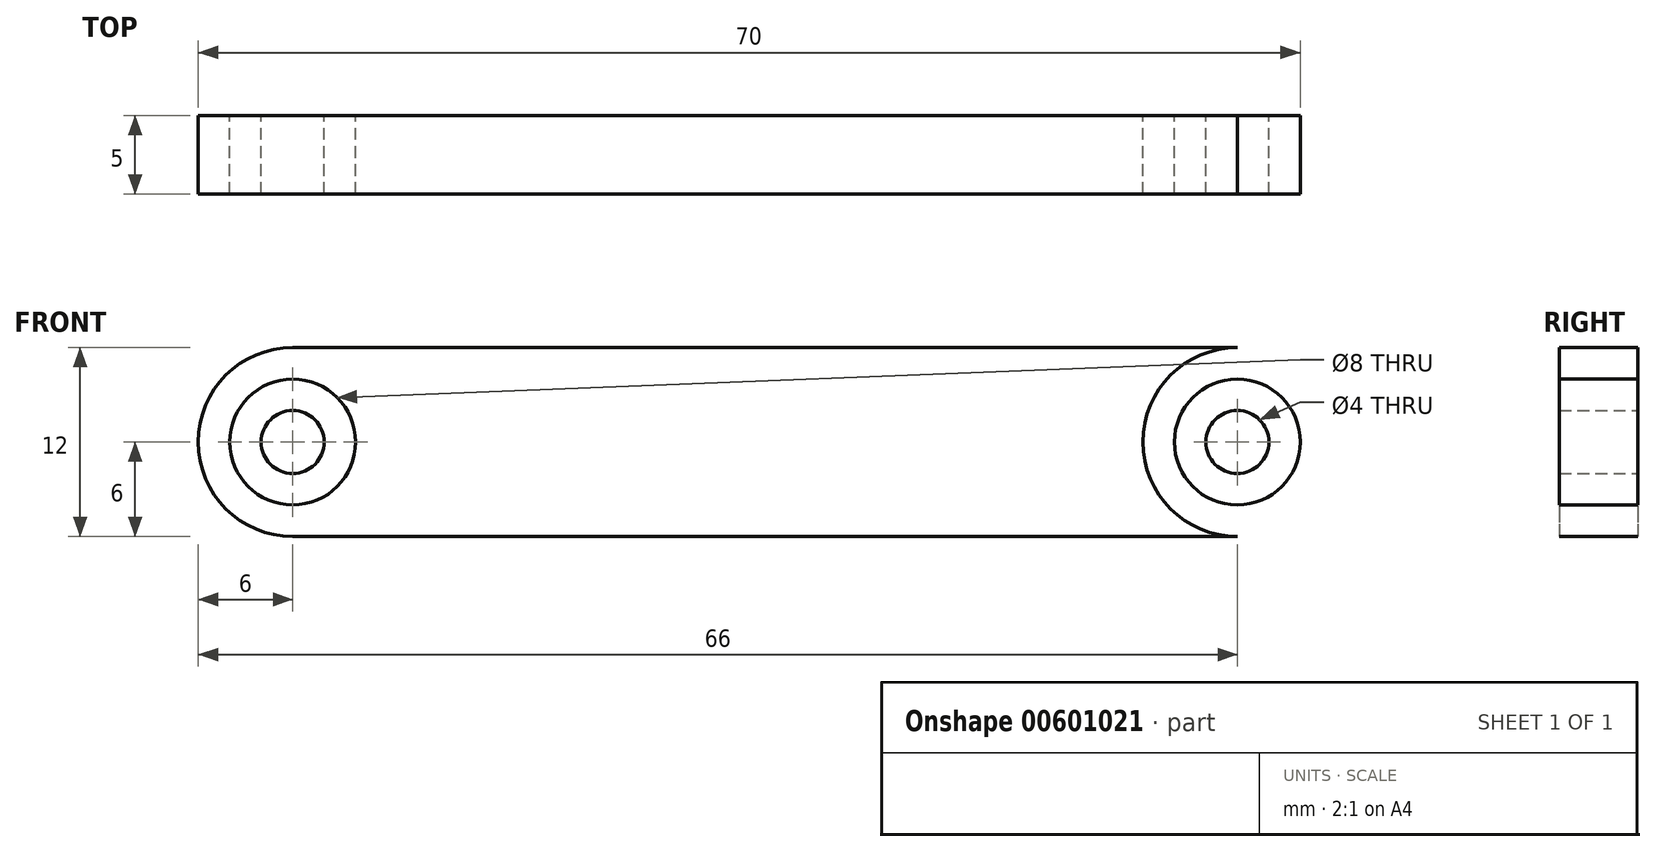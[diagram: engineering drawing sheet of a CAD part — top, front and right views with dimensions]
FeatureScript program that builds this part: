
annotation { "Feature Type Name" : "Feature", "Feature Type Description" : "" }
export const myFeature = defineFeature(function(context is Context, id is Id, definition is map)
    precondition{}
    {
        {
            var Q0;
            Q0=qCreatedBy(makeId("Front.planeOp"),FACE);
            var sketch = newSketch(context, id + "F0", { "sketchPlane" : qUnion([Q0])});
            skCircle(sketch, "E0", {"center": v(-30, 0) * mm, "radius": 6 * mm});
            skCircle(sketch, "E1", {"center": v(-30, 0) * mm, "radius": 2 * mm});
            skCircle(sketch, "E2", {"center": v(-30, 0) * mm, "radius": 4 * mm});
            skLineSegment(sketch, "E3", {"start": v(-30, 6) * mm, "end": v(0, 6) * mm});
            skLineSegment(sketch, "E4", {"start": v(-30, -6) * mm, "end": v(0, -6) * mm});
            skCircle(sketch, "E5.MirrorC", {"center": v(30, 0) * mm, "radius": 6 * mm});
            skCircle(sketch, "E6.MirrorC", {"center": v(30, 0) * mm, "radius": 2 * mm});
            skLineSegment(sketch, "E7.MirrorCS", {"start": v(30, 6) * mm, "end": v(0, 6) * mm});
            skLineSegment(sketch, "E8.MirrorCS", {"start": v(30, -6) * mm, "end": v(0, -6) * mm});
            skCircle(sketch, "E9.MirrorC", {"center": v(30, 0) * mm, "radius": 4 * mm});
            skSolve(sketch);
        }
        {
            var Q0;
            Q0=makeQuery(id+"F0.imprint","IMPRINT",FACE,{"disambiguationData":[TD([[makeQuery(id+"F0.imprint","IMPRINT",EDGE,{"derivedFrom":sQuery(id+"F0.wireOp",EDGE,"E1")}),1.0]])]});
            var Q1;
            Q1=makeQuery(id+"F0.imprint","IMPRINT",FACE,{"disambiguationData":[TD([[makeQuery(id+"F0.imprint","IMPRINT",EDGE,{"derivedFrom":sQuery(id+"F0.wireOp",EDGE,"E2")}),-1.0]])]});
            var Q2;
            {var subQ4=sQuery(id+"F0.wireOp",EDGE,"E3");Q2=makeQuery(id+"F0.imprint","IMPRINT",FACE,{"disambiguationData":[TD([[makeQuery(id+"F0.imprint","IMPRINT",EDGE,{"derivedFrom":subQ4}),-1.0]])]});}
            var Q3;
            Q3=makeQuery(id+"F0.imprint","IMPRINT",FACE,{"disambiguationData":[TD([[makeQuery(id+"F0.imprint","IMPRINT",EDGE,{"derivedFrom":sQuery(id+"F0.wireOp",EDGE,"E9.MirrorC")}),1.0]])]});
            var Q4;
            Q4=makeQuery(id+"F0.imprint","IMPRINT",FACE,{"disambiguationData":[TD([[makeQuery(id+"F0.imprint","IMPRINT",EDGE,{"derivedFrom":sQuery(id+"F0.wireOp",EDGE,"E6.MirrorC")}),-1.0]])]});
            extrude(context, id + "F1", {"entities" : qUnion([Q0, Q1, Q2, Q3, Q4]), "depth" : 5 * mm, "offsetDistance" : 25 * mm});
        }
    });
